# Revit family: 14.Регулирующая заслонка для прямоугольных каналов ZR
name_source: partatom
category: Оборудование
revit_build: Autodesk Revit 2016 (Build: 20151209_0715(x64)
units: mm (PartAtom-declared; Revit-internal decimal feet)

## family parameters
Всегда вертикально = Да
На основе рабочей плоскости = Нет
Общий = Нет
При загрузке вырезать с полостями = Нет
Размер круглого соединителя = Использовать диаметр
Тип детали = Нормальный
Точка расчета площади = Нет

## types (10) — shared parameters
Глубина среза = 15 мм
Единица измерения = шт.
Завод изготовитель = KORF
Ключевая пометка = Вентиляция
Материал = Сталь серая
Наименование и тех.хар-ка = Регулирующая заслонка для прямоугольных каналов
Отступ = 20 мм
Раздел = ОВ

## per-type parameters (varying)
| type | H | L ламели | N | А | Б | Высота | Г | Д | Е | Ж | И | Масса единицы | Размер В | Тип, марка, обозначение | Толщина ламели | Ширина | Электропривод | х | ширина ламели |
| 30-15 | 101 мм | 300 мм | 3 | 300 мм | 150 мм | 150 мм | 170 мм | 340 мм | 190 мм | 9 мм | 178 мм | 3.8 кг | 320 мм | ZR 30-15 | 3 мм | 300 мм | Нет | 2 мм | 49 мм |
| 40-20 | 134 мм | 400 мм | 0 | 400 мм | 200 мм | 200 мм | 220 мм | 440 мм | 240 мм | 9 мм | 178 мм | 5.4 кг | 420 мм | ZR 40-20 | 4 мм | 400 мм | Да | 2 мм | 66 мм |
| 50-25 | 168 мм | 500 мм | 0 | 500 мм | 250 мм | 250 мм | 270 мм | 540 мм | 290 мм | 9 мм | 178 мм | 6.6 кг | 520 мм | ZR 50-25 | 5 мм | 500 мм | Да | 3 мм | 82 мм |
| 50-30 | 201 мм | 500 мм | 0 | 500 мм | 300 мм | 300 мм | 320 мм | 540 мм | 340 мм | 9 мм | 178 мм | 7.6 кг | 520 мм | ZR 50-30 | 6 мм | 500 мм | Да | 3 мм | 99 мм |
| 60-30 | 201 мм | 600 мм | 0 | 600 мм | 300 мм | 300 мм | 320 мм | 640 мм | 340 мм | 9 мм | 178 мм | 8.6 кг | 620 мм | ZR 60-30 | 6 мм | 600 мм | Да | 3 мм | 99 мм |
| 60-35 | 234 мм | 600 мм | 0 | 600 мм | 350 мм | 350 мм | 370 мм | 640 мм | 390 мм | 9 мм | 178 мм | 9 кг | 620 мм | ZR 60-35 | 7 мм | 600 мм | Да | 4 мм | 116 мм |
| 70-40 | 268 мм | 700 мм | 0 | 700 мм | 400 мм | 400 мм | 420 мм | 740 мм | 440 мм | 9 мм | 178 мм | 11.2 кг | 720 мм | ZR 70-40 | 8 мм | 700 мм | Да | 4 мм | 132 мм |
| 80-50 | 334 мм | 800 мм | 0 | 800 мм | 500 мм | 500 мм | 520 мм | 870 мм | 540 мм | 9 мм | 178 мм | 13.6 кг | 820 мм | ZR 80-50 | 10 мм | 800 мм | Да | 5 мм | 166 мм |
| 90-50 | 334 мм | 900 мм | 0 | 900 мм | 500 мм | 500 мм | 530 мм | 960 мм | 560 мм | 11 мм | 190 мм | 15.8 кг | 930 мм | ZR 90-50 | 10 мм | 900 мм | Да | 5 мм | 166 мм |
| 100-50 | 334 мм | 1000 мм | 0 | 1000 мм | 500 мм | 500 мм | 530 мм | 1060 мм | 560 мм | 11 мм | 190 мм | 16.8 кг | 1030 мм | ZR 100-50 | 10 мм | 1000 мм | Да | 5 мм | 166 мм |
